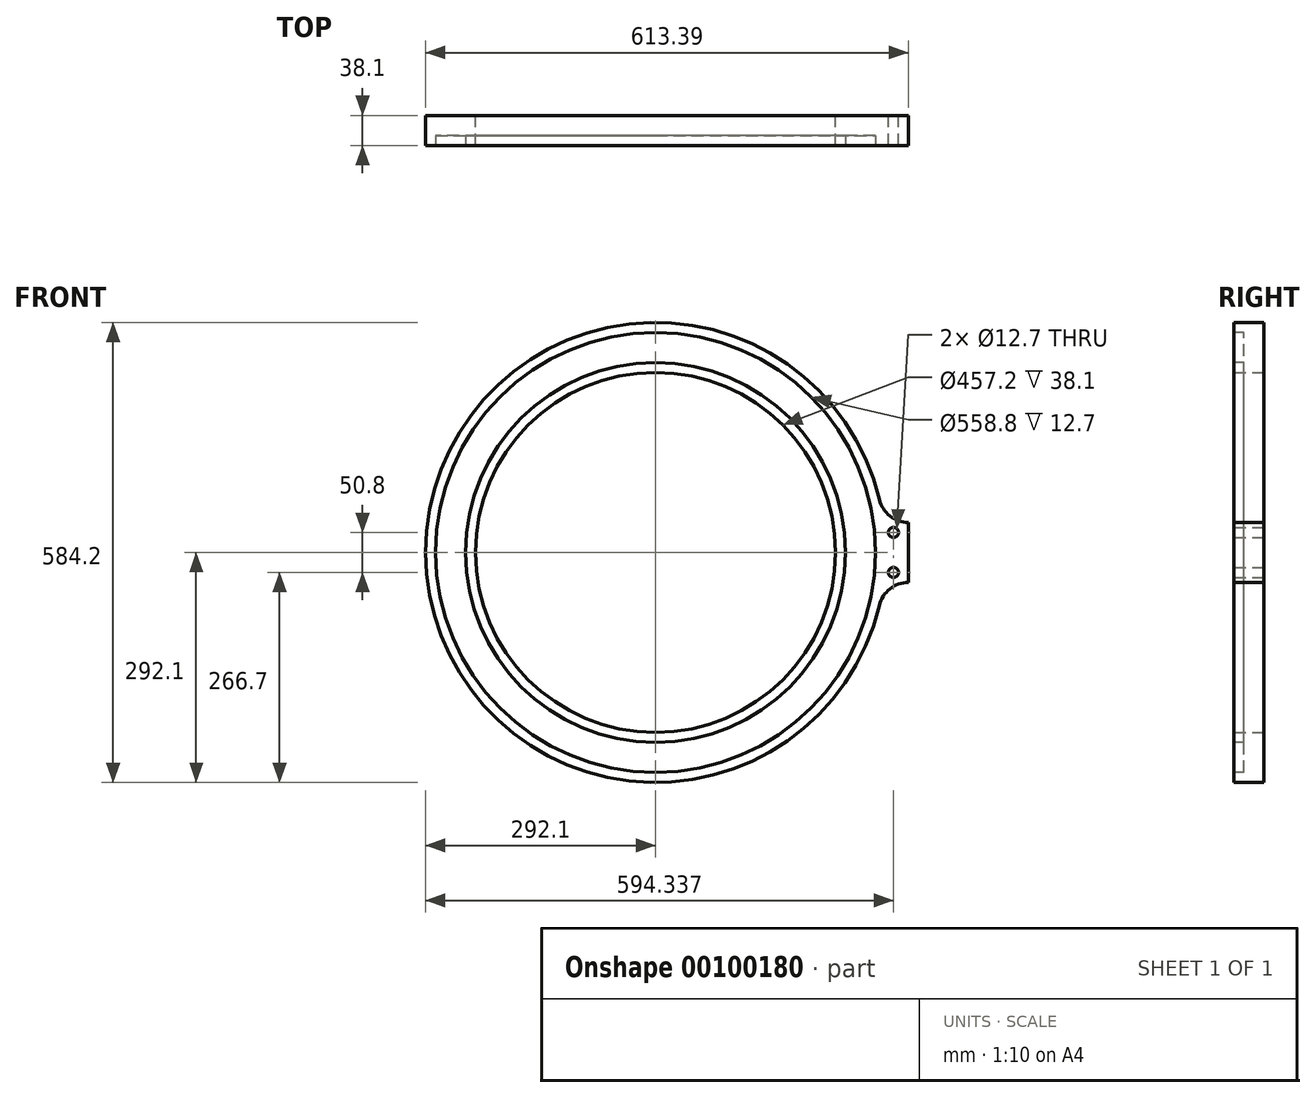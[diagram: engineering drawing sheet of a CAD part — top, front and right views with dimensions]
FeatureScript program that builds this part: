
annotation { "Feature Type Name" : "Feature", "Feature Type Description" : "" }
export const myFeature = defineFeature(function(context is Context, id is Id, definition is map)
    precondition{}
    {
        {
            var Q0;
            Q0=qCreatedBy(makeId("Front.planeOp"),FACE);
            var sketch = newSketch(context, id + "F0", { "sketchPlane" : qUnion([Q0])});
            skCircle(sketch, "E0", {"center": v(-444.5, 0) * mm, "radius": 228.6 * mm});
            skArc(sketch, "E1.0", {"start": v(-160.28, 67.4) * mm, "mid": v(-736.6, 0) * mm, "end": v(-160.28, -67.4) * mm});
            skLineSegment(sketch, "E2", {"start": v(-123.21, 38.1) * mm, "end": v(0, 38.1) * mm});
            skLineSegment(sketch, "E3", {"start": v(-123.21, -38.1) * mm, "end": v(0, -38.1) * mm});
            skPoint(sketch, "E4.visualSharp", {"position": v(-154.9, 38.1) * mm});
            skArc(sketch, "E4.filletArc", {"start": v(-160.28, 67.4) * mm, "mid": v(-146.84, 46.31) * mm, "end": v(-123.21, 38.1) * mm});
            skPoint(sketch, "E5.visualSharp", {"position": v(-154.9, -38.1) * mm});
            skArc(sketch, "E5.filletArc", {"start": v(-123.21, -38.1) * mm, "mid": v(-146.84, -46.31) * mm, "end": v(-160.28, -67.4) * mm});
            skLineSegment(sketch, "E6", {"start": v(-123.21, 38.1) * mm, "end": v(-123.21, -38.1) * mm});
            skCircle(sketch, "E7", {"center": v(-142.26, 25.4) * mm, "radius": 6.35 * mm});
            skCircle(sketch, "E8", {"center": v(-142.26, -25.4) * mm, "radius": 6.35 * mm});
            skSolve(sketch);
        }
        {
            var Q0;
            Q0=makeQuery(id+"F0.imprint","IMPRINT",FACE,{"disambiguationData":[TD([[makeQuery(id+"F0.imprint","IMPRINT",EDGE,{"derivedFrom":sQuery(id+"F0.wireOp",EDGE,"E0")}),-1.0]])]});
            extrude(context, id + "F1", {"entities" : qUnion([Q0]), "endBound" : BoundingType.SYMMETRIC, "depth" : 38.1 * mm});
        }
        {
            var Q0;
            Q0=makeQuery(id+"F1.opExtrude","CAP_FACE",FACE,{"disambiguationData":[OSD([sQuery(id+"F0.wireOp",EDGE,"E0"),sQuery(id+"F0.wireOp",EDGE,"E1.0"),sQuery(id+"F0.wireOp",EDGE,"E4.filletArc"),sQuery(id+"F0.wireOp",EDGE,"E5.filletArc"),sQuery(id+"F0.wireOp",EDGE,"E6"),sQuery(id+"F0.wireOp",EDGE,"E7"),sQuery(id+"F0.wireOp",EDGE,"E8")])],"isStart":false});
            var sketch = newSketch(context, id + "F2", { "sketchPlane" : qUnion([Q0])});
            skCircle(sketch, "E9.0", {"center": v(-444.5, 0) * mm, "radius": 241.3 * mm});
            skCircle(sketch, "E10.converted", {"center": v(-444.5, 0) * mm, "radius": 279.4 * mm});
            skSolve(sketch);
        }
        {
            var Q0;
            Q0=makeQuery(id+"F2.imprint","IMPRINT",FACE,{"disambiguationData":[TD([[makeQuery(id+"F2.imprint","IMPRINT",EDGE,{"derivedFrom":sQuery(id+"F2.wireOp",EDGE,"E9.0")}),-1.0]])]});
            extrude(context, id + "F3", {"entities" : qUnion([Q0]), "operationType" : NewBodyOperationType.REMOVE, "oppositeDirection" : true, "depth" : 12.7 * mm});
        }
    });
